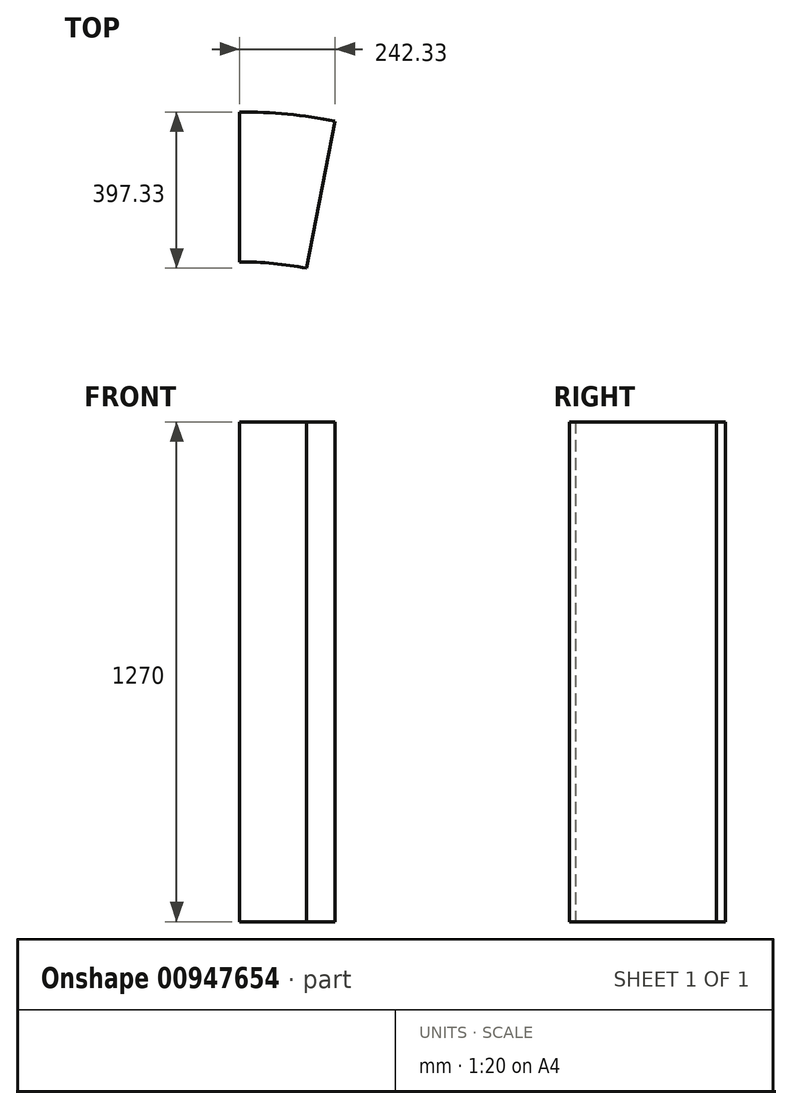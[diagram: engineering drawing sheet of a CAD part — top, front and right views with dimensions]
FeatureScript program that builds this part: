
annotation { "Feature Type Name" : "Feature", "Feature Type Description" : "" }
export const myFeature = defineFeature(function(context is Context, id is Id, definition is map)
    precondition{}
    {
        {
            var Q0;
            Q0=qCreatedBy(makeId("Top.planeOp"),FACE);
            var sketch = newSketch(context, id + "F0", { "sketchPlane" : qUnion([Q0])});
            skCircle(sketch, "E0", {"center": v(0, 0) * mm, "radius": 1270 * mm});
            skCircle(sketch, "E1", {"center": v(0, 0) * mm, "radius": 889 * mm});
            skSolve(sketch);
        }
        {
            var Q0;
            Q0=qCreatedBy(makeId("Top.planeOp"),FACE);
            var sketch = newSketch(context, id + "F1", { "sketchPlane" : qUnion([Q0])});
            skLineSegment(sketch, "E2", {"start": v(0, 1270) * mm, "end": v(0, 889) * mm});
            skLineSegment(sketch, "E3", {"start": v(169.63, 872.67) * mm, "end": v(242.33, 1246.67) * mm});
            skArc(sketch, "E4.0", {"start": v(242.33, 1246.67) * mm, "mid": v(121.72, 1264.15) * mm, "end": v(0, 1270) * mm});
            skArc(sketch, "E5.0", {"start": v(169.63, 872.67) * mm, "mid": v(85.2, 884.9) * mm, "end": v(0, 889) * mm});
            skSolve(sketch);
        }
        {
            var Q0;
            Q0 = qSketchRegion(id + "F1", true);
            extrude(context, id + "F2", {"entities" : qUnion([Q0]), "depth" : 1270 * mm, "offsetDistance" : 25.4 * mm});
        }
    });
